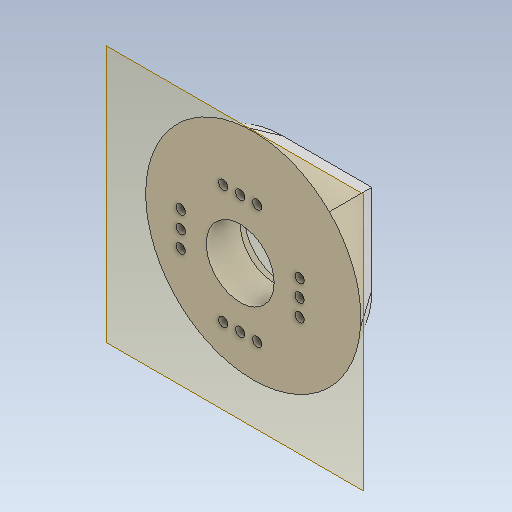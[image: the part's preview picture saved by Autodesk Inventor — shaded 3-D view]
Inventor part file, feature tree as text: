
AUTODESK INVENTOR PART (.ipt)
format: ipt  version: 2020 (Build 240168000, 168)  size: 175,104 bytes
history: native  units: mm
features: sketch x4, other x4, hole x2, reference x2, plane x1, loft x1
ambient origin geometry x8: Origin, YZ Plane, XZ Plane, XY Plane, X Axis, Y Axis, Z Axis, Center Point
bodies: Solid1 (feature_tree)
feature tree (14):
  sketch  "Sketch1"  dims[d0=21.0mm d1=10.0mm]
  plane  "Work Plane1"
  loft  "Loft1"
  hole  "Hole1"  [1 undecoded]
  hole  "Hole2"  [1 undecoded]
  reference  "Reference1"
  reference  "Reference2"
  sketch  "Sketch2"  dims[d2=10.0mm d3=5.0mm]
  sketch  "Sketch3"  dims[d4=0.0mm d5=90.0deg d6=0.0mm d7=90.0deg]
  sketch  "Sketch4"  dims[d8=8.0mm d9=6.0mm d10=9.0mm d11=1.0mm d12=90.0deg d13=8.0mm d14=20.594885mm d15=7.0mm d16=2.0mm d17=2.0mm d18=40.0mm d20=360.0deg d22=1.1mm d23=6.0mm d24=9.0mm d25=1.0mm d26=90.0deg d27=8.0mm d28=20.594885mm d29=0.75mm d30=20.594885mm d31=0.0625mm d32=0.75mm d33=0.375mm]
  parser-record x1  (decoder bookkeeping rows leaked as tree rows — omitted from the tree; the rows remain in map.json)
  other  "motorized.iam"
  other  "leg:1"
  other  "bracket:1"
note: 2 required parameter values undecoded (feature->parameter linkage not recoverable at this tier; creation-order binding heuristic only, values carry confidence <= 0.55)
note: 1 file-system path scrubbed to <path> (originals preserved in map.json)
